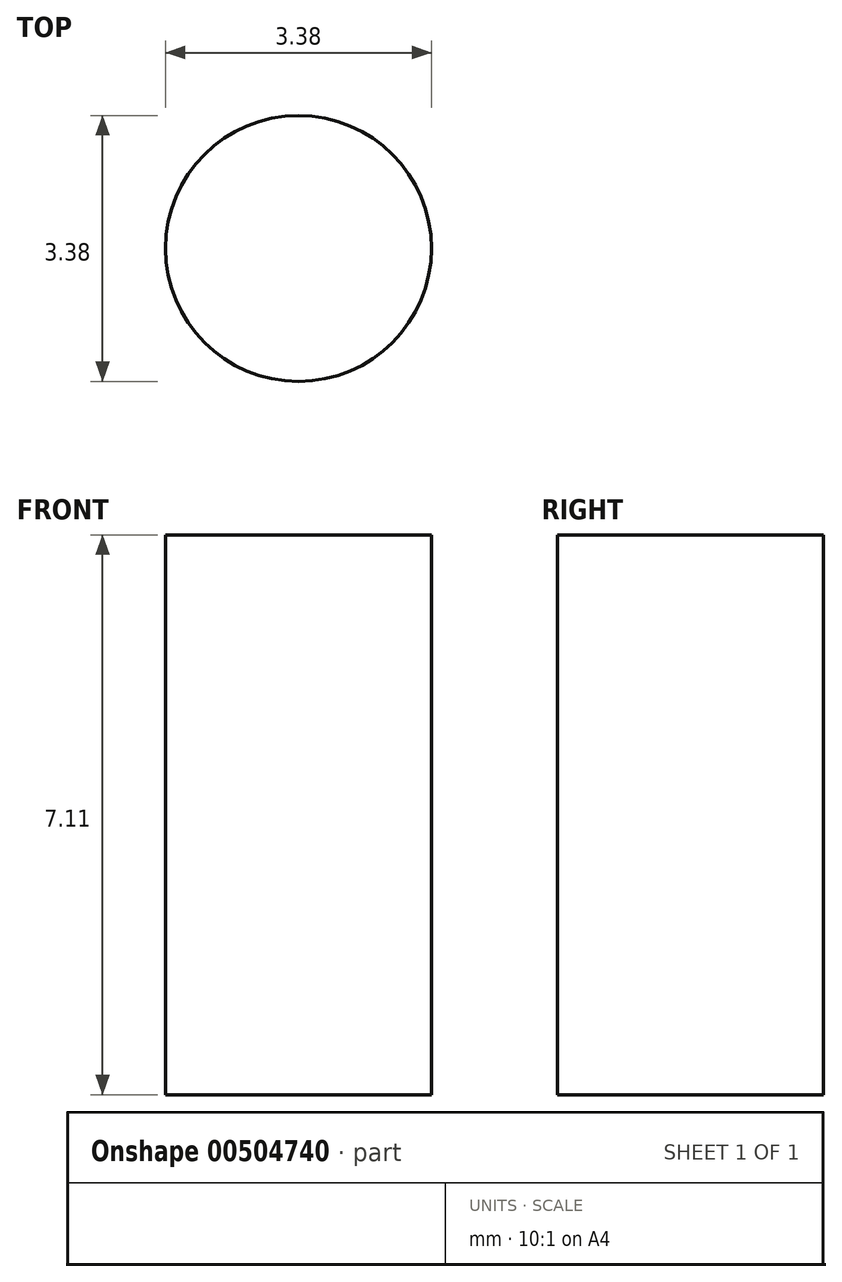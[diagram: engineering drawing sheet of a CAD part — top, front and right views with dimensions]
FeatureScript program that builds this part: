
annotation { "Feature Type Name" : "Feature", "Feature Type Description" : "" }
export const myFeature = defineFeature(function(context is Context, id is Id, definition is map)
    precondition{}
    {
        {
            var Q0;
            Q0=qCreatedBy(makeId("Top.planeOp"),FACE);
            var sketch = newSketch(context, id + "F0", { "sketchPlane" : qUnion([Q0])});
            skCircle(sketch, "E0", {"center": v(0, 0) * mm, "radius": 1.69 * mm});
            skSolve(sketch);
        }
        {
            var Q0;
            Q0=qSketchRegion(id+"F0",true);
            var Q1;
            Q1=makeQuery(id+"F0.imprint","IMPRINT",FACE,{"disambiguationData":[TD([[makeQuery(id+"F0.imprint","IMPRINT",EDGE,{"derivedFrom":sQuery(id+"F0.wireOp",EDGE,"E0")}),1.0]])]});
            extrude(context, id + "F1", {"entities" : qUnion([Q0, Q1]), "depth" : 7.11 * mm});
        }
    });
